# Revit family: RBA4110-924
name_source: partatom
category: Plumbing Fixtures
units: mm (PartAtom-declared; Revit-internal decimal feet)

## family parameters
Always vertical = Yes
Cut with Voids When Loaded = No
Part Type = Normal
Room Calculation Point = No
Round Connector Dimension = Use Diameter
Shared = No
Work Plane-Based = No

## types (2) — shared parameters
Diameter = 32 mm  [stored 0.104987 ft]
Horizontal Rail = Yes
Manufacturer = RBA Group
Materials & Finishes = #304 Stainless Steel, Satin Finish
URL = www.rba.com.au
zero-valued in all types: Default Elevation

## per-type parameters (varying)
| type | Description | Left Hand Rail | Model | Right Hand Rail |
| RBA4801-711-LH | RTA SSS T-Rail Left Hand | Yes | RBA4110-924-LH | No |
| RBA4801-711-RH | RTA SSS T-Rail Right Hand | No | RBA4110-924-RH | Yes |

note: [stored X ft] marks values corroborated as IEEE doubles in the binary element streams (Revit-internal decimal feet)

## geometry (parser evidence)
native form markers: Blend x35, Sweep x3
no freeform markers — native parametric forms only
